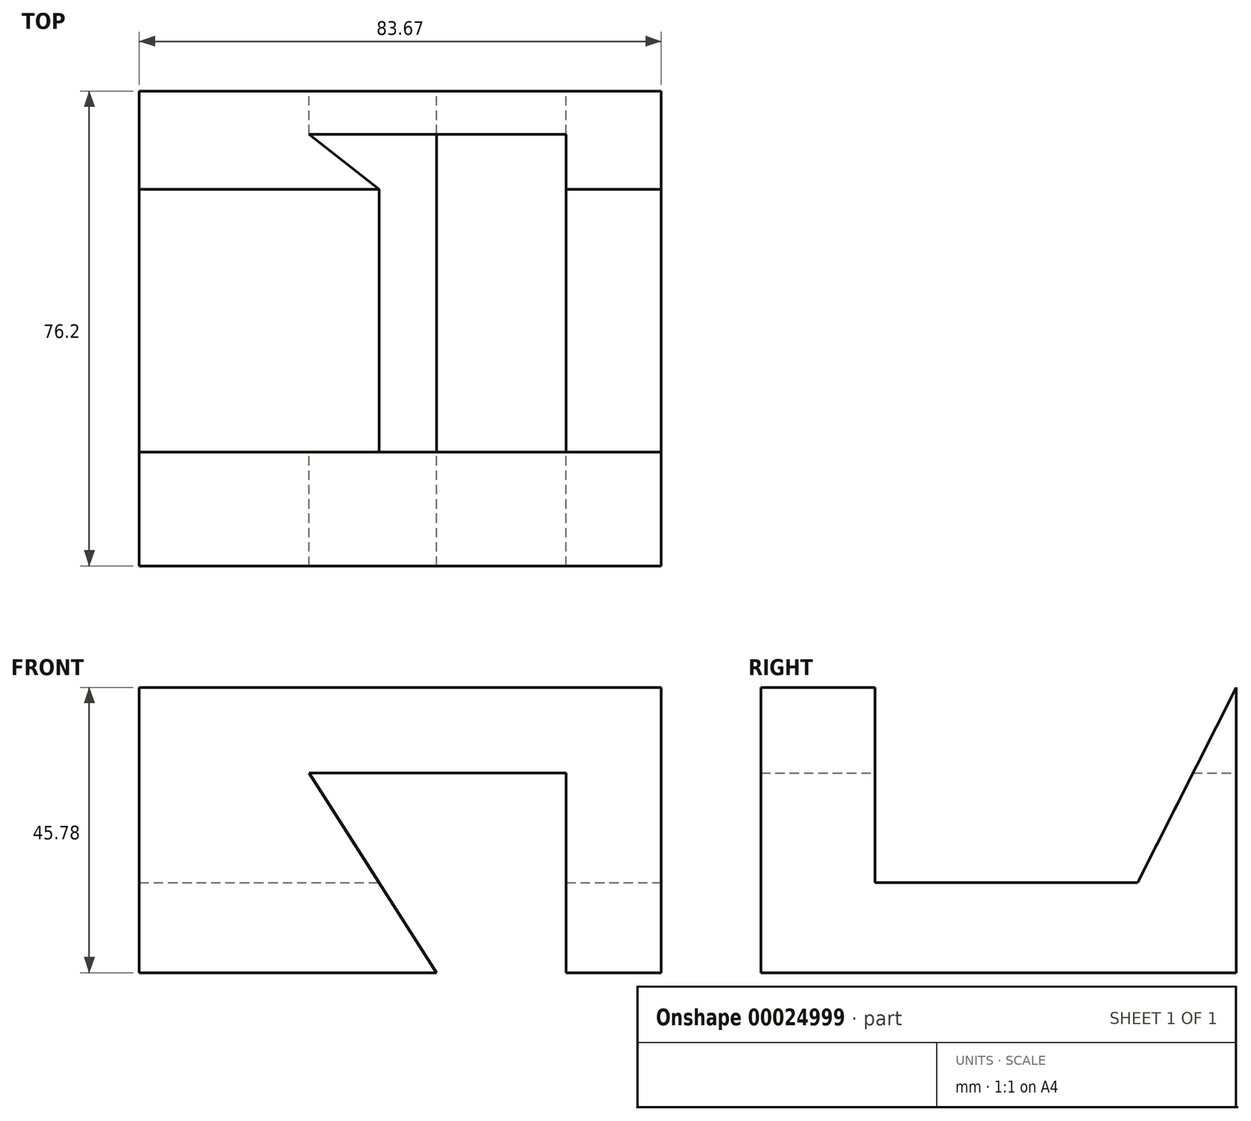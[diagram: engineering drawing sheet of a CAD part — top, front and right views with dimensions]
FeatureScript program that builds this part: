
annotation { "Feature Type Name" : "Feature", "Feature Type Description" : "" }
export const myFeature = defineFeature(function(context is Context, id is Id, definition is map)
    precondition{}
    {
        {
            var Q0;
            Q0=qCreatedBy(makeId("Front.planeOp"),FACE);
            var sketch = newSketch(context, id + "F0", { "sketchPlane" : qUnion([Q0])});
            skLineSegment(sketch, "E0", {"start": v(0, 0) * mm, "end": v(47.68, 0) * mm});
            skLineSegment(sketch, "E1", {"start": v(47.68, 0) * mm, "end": v(27.2, 32.03) * mm});
            skLineSegment(sketch, "E2", {"start": v(27.2, 32.03) * mm, "end": v(68.45, 32.03) * mm});
            skLineSegment(sketch, "E3", {"start": v(68.45, 32.03) * mm, "end": v(68.45, 0) * mm});
            skLineSegment(sketch, "E4", {"start": v(68.45, 0) * mm, "end": v(83.67, 0) * mm});
            skLineSegment(sketch, "E5", {"start": v(83.67, 0) * mm, "end": v(83.67, 45.78) * mm});
            skLineSegment(sketch, "E6", {"start": v(83.67, 45.78) * mm, "end": v(0, 45.78) * mm});
            skLineSegment(sketch, "E7", {"start": v(0, 45.78) * mm, "end": v(0, 0) * mm});
            skSolve(sketch);
        }
        {
            var Q0;
            Q0=makeQuery(id+"F0.imprint","IMPRINT",FACE,{"disambiguationData":[TD([[makeQuery(id+"F0.imprint","IMPRINT",EDGE,{"derivedFrom":sQuery(id+"F0.wireOp",EDGE,"E0")}),1.0]])]});
            extrude(context, id + "F1", {"entities" : qUnion([Q0]), "depth" : 76.2 * mm});
        }
        {
            var Q0;
            Q0=makeQuery(id+"F1.opExtrude","SWEPT_FACE",FACE,{"disambiguationData":[OSD([sQuery(id+"F0.wireOp",EDGE,"E5")])]});
            var sketch = newSketch(context, id + "F2", { "sketchPlane" : qUnion([Q0])});
            skLineSegment(sketch, "E8", {"start": v(-57.92, 45.78) * mm, "end": v(-57.92, 14.48) * mm});
            skLineSegment(sketch, "E9", {"start": v(-57.92, 14.48) * mm, "end": v(-15.8, 14.48) * mm});
            skLineSegment(sketch, "E10", {"start": v(-15.8, 14.48) * mm, "end": v(0, 45.78) * mm});
            skLineSegment(sketch, "E11", {"start": v(0, 45.78) * mm, "end": v(-57.92, 45.78) * mm});
            skSolve(sketch);
        }
        {
            var Q0;
            Q0=makeQuery(id+"F2.imprint","IMPRINT",FACE,{"disambiguationData":[TD([[makeQuery(id+"F2.imprint","IMPRINT",EDGE,{"derivedFrom":sQuery(id+"F2.wireOp",EDGE,"E8")}),1.0]])]});
            extrude(context, id + "F3", {"entities" : qUnion([Q0]), "operationType" : NewBodyOperationType.REMOVE, "endBound" : BoundingType.THROUGH_ALL, "oppositeDirection" : true, "depth" : 25.4 * mm});
        }
    });
